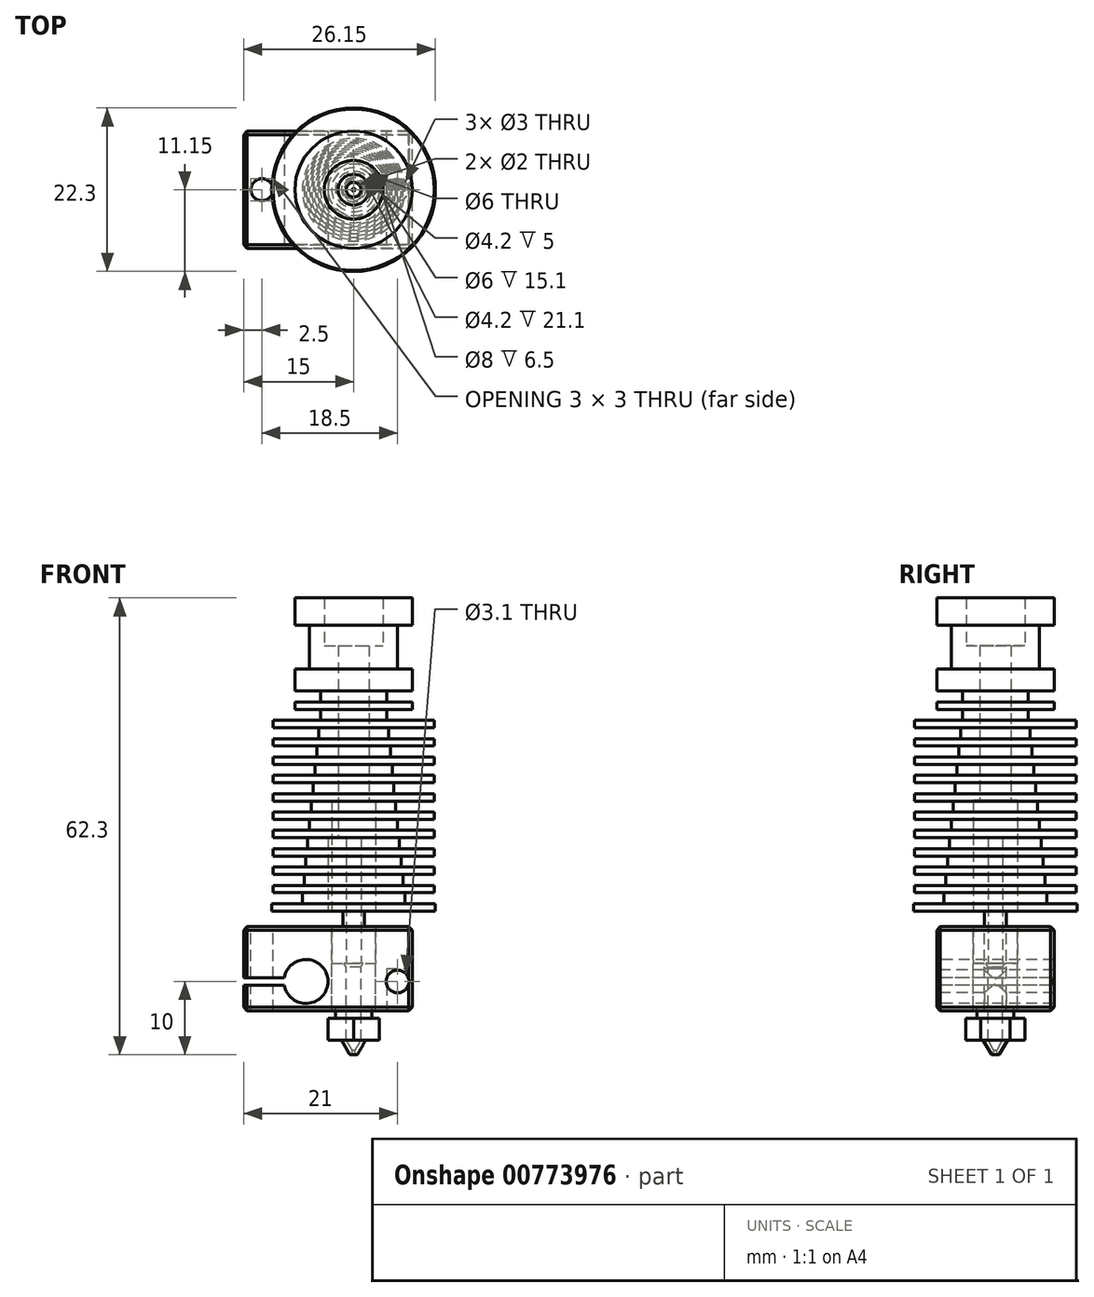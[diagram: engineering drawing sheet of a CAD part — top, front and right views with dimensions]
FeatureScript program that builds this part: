
annotation { "Feature Type Name" : "Feature", "Feature Type Description" : "" }
export const myFeature = defineFeature(function(context is Context, id is Id, definition is map)
    precondition{}
    {
        {
            var Q0;
            Q0=qCreatedBy(makeId("Front.planeOp"),FACE);
            var sketch = newSketch(context, id + "F0", { "sketchPlane" : qUnion([Q0])});
            skLineSegment(sketch, "E0", {"start": v(0, 0) * mm, "end": v(0, 45.21) * mm, "construction": true});
            skLineSegment(sketch, "E1", {"start": v(-3, 0) * mm, "end": v(-3, 15.1) * mm});
            skLineSegment(sketch, "E2", {"start": v(-3, 15.1) * mm, "end": v(-2.1, 15.1) * mm});
            skLineSegment(sketch, "E3", {"start": v(-2.1, 36.2) * mm, "end": v(-4, 36.2) * mm});
            skLineSegment(sketch, "E4", {"start": v(-4, 36.2) * mm, "end": v(-4, 42.7) * mm});
            skLineSegment(sketch, "E5", {"start": v(-4, 42.7) * mm, "end": v(-8, 42.7) * mm});
            skLineSegment(sketch, "E6", {"start": v(-8, 42.7) * mm, "end": v(-8, 39) * mm});
            skLineSegment(sketch, "E7", {"start": v(-6, 39) * mm, "end": v(-6, 33) * mm});
            skLineSegment(sketch, "E8", {"start": v(-6, 33) * mm, "end": v(-8, 33) * mm});
            skLineSegment(sketch, "E9", {"start": v(-8, 33) * mm, "end": v(-8, 30) * mm});
            skLineSegment(sketch, "E10", {"start": v(-8, 30) * mm, "end": v(-4.5, 30) * mm});
            skLineSegment(sketch, "E11", {"start": v(-4.5, 28.5) * mm, "end": v(-8, 28.5) * mm});
            skLineSegment(sketch, "E12", {"start": v(-8, 28.5) * mm, "end": v(-8, 27.5) * mm});
            skLineSegment(sketch, "E13", {"start": v(-8, 27.5) * mm, "end": v(-4.5, 27.5) * mm});
            skLineSegment(sketch, "E14", {"start": v(-4.5, 30) * mm, "end": v(-4.5, 28.5) * mm});
            skLineSegment(sketch, "E15", {"start": v(-8, 39) * mm, "end": v(-6, 39) * mm});
            skLineSegment(sketch, "E16", {"start": v(-2.1, 15.1) * mm, "end": v(-2.1, 36.2) * mm});
            skLineSegment(sketch, "E17", {"start": v(-11.15, 1) * mm, "end": v(-7, 1) * mm});
            skLineSegment(sketch, "E18", {"start": v(-7, 1) * mm, "end": v(-7, 2.5) * mm});
            skLineSegment(sketch, "E19", {"start": v(-7, 2.5) * mm, "end": v(-11, 2.5) * mm});
            skLineSegment(sketch, "E20", {"start": v(-11, 2.5) * mm, "end": v(-11, 3.5) * mm});
            skLineSegment(sketch, "E21", {"start": v(-11, 3.5) * mm, "end": v(-6.75, 3.5) * mm});
            skLineSegment(sketch, "E22", {"start": v(-6.75, 3.5) * mm, "end": v(-6.75, 5) * mm});
            skLineSegment(sketch, "E23", {"start": v(-6.75, 5) * mm, "end": v(-11, 5) * mm});
            skLineSegment(sketch, "E24", {"start": v(-11, 5) * mm, "end": v(-11, 6) * mm});
            skLineSegment(sketch, "E25", {"start": v(-11, 6) * mm, "end": v(-6.5, 6) * mm});
            skLineSegment(sketch, "E26", {"start": v(-6.5, 6) * mm, "end": v(-6.5, 7.5) * mm});
            skLineSegment(sketch, "E27", {"start": v(-6.5, 7.5) * mm, "end": v(-11, 7.5) * mm});
            skLineSegment(sketch, "E28", {"start": v(-11, 7.5) * mm, "end": v(-11, 8.5) * mm});
            skLineSegment(sketch, "E29", {"start": v(-11, 8.5) * mm, "end": v(-6.25, 8.5) * mm});
            skLineSegment(sketch, "E30", {"start": v(-6.25, 8.5) * mm, "end": v(-6.25, 10) * mm});
            skLineSegment(sketch, "E31", {"start": v(-6.25, 10) * mm, "end": v(-11, 10) * mm});
            skLineSegment(sketch, "E32", {"start": v(-11, 10) * mm, "end": v(-11, 11) * mm});
            skLineSegment(sketch, "E33", {"start": v(-11, 11) * mm, "end": v(-6, 11) * mm});
            skLineSegment(sketch, "E34", {"start": v(-6, 11) * mm, "end": v(-6, 12.5) * mm});
            skLineSegment(sketch, "E35", {"start": v(-6, 12.5) * mm, "end": v(-11, 12.5) * mm});
            skLineSegment(sketch, "E36", {"start": v(-11, 12.5) * mm, "end": v(-11, 13.5) * mm});
            skLineSegment(sketch, "E37", {"start": v(-11, 13.5) * mm, "end": v(-5.75, 13.5) * mm});
            skLineSegment(sketch, "E38", {"start": v(-5.75, 13.5) * mm, "end": v(-5.75, 15) * mm});
            skLineSegment(sketch, "E39", {"start": v(-5.75, 15) * mm, "end": v(-11, 15) * mm});
            skLineSegment(sketch, "E40", {"start": v(-11, 15) * mm, "end": v(-11, 16) * mm});
            skLineSegment(sketch, "E41", {"start": v(-11, 16) * mm, "end": v(-5.5, 16) * mm});
            skLineSegment(sketch, "E42", {"start": v(-5.5, 16) * mm, "end": v(-5.5, 17.5) * mm});
            skLineSegment(sketch, "E43", {"start": v(-5.5, 17.5) * mm, "end": v(-11, 17.5) * mm});
            skLineSegment(sketch, "E44", {"start": v(-11, 17.5) * mm, "end": v(-11, 18.5) * mm});
            skLineSegment(sketch, "E45", {"start": v(-11, 18.5) * mm, "end": v(-5.25, 18.5) * mm});
            skLineSegment(sketch, "E46", {"start": v(-5.25, 18.5) * mm, "end": v(-5.25, 20) * mm});
            skLineSegment(sketch, "E47", {"start": v(-5.25, 20) * mm, "end": v(-11, 20) * mm});
            skLineSegment(sketch, "E48", {"start": v(-11, 20) * mm, "end": v(-11, 21) * mm});
            skLineSegment(sketch, "E49", {"start": v(-11, 21) * mm, "end": v(-5, 21) * mm});
            skLineSegment(sketch, "E50", {"start": v(-5, 21) * mm, "end": v(-5, 22.5) * mm});
            skLineSegment(sketch, "E51", {"start": v(-5, 22.5) * mm, "end": v(-11, 22.5) * mm});
            skLineSegment(sketch, "E52", {"start": v(-11, 22.5) * mm, "end": v(-11, 23.5) * mm});
            skLineSegment(sketch, "E53", {"start": v(-11, 23.5) * mm, "end": v(-4.75, 23.5) * mm});
            skLineSegment(sketch, "E54", {"start": v(-4.75, 23.5) * mm, "end": v(-4.75, 25) * mm});
            skLineSegment(sketch, "E55", {"start": v(-4.75, 25) * mm, "end": v(-11, 25) * mm});
            skLineSegment(sketch, "E56", {"start": v(-11, 25) * mm, "end": v(-11, 26) * mm});
            skLineSegment(sketch, "E57", {"start": v(-11, 26) * mm, "end": v(-4.5, 26) * mm});
            skLineSegment(sketch, "E58", {"start": v(-4.5, 26) * mm, "end": v(-4.5, 27.5) * mm});
            skLineSegment(sketch, "E59", {"start": v(-3, 0) * mm, "end": v(-11.15, 0) * mm});
            skLineSegment(sketch, "E60", {"start": v(-11.15, 0) * mm, "end": v(-11.15, 1) * mm});
            skSolve(sketch);
        }
        {
            var Q0;
            Q0 = qSketchRegion(id + "F0", true);
            var Q1;
            Q1=sQuery(id+"F0.wireOp",EDGE,"E0");
            revolve(context, id + "F1", {"surfaceOperationType" : NewSurfaceOperationType.NEW, "entities" : qUnion([Q0]), "axis" : qUnion([Q1]), "revolveType" : RevolveType.FULL});
        }
        {
            var Q0;
            Q0=qCreatedBy(makeId("Front.planeOp"),FACE);
            var sketch = newSketch(context, id + "F2", { "sketchPlane" : qUnion([Q0])});
            skLineSegment(sketch, "E61", {"start": v(0, 0) * mm, "end": v(0, 46.31) * mm, "construction": true});
            skLineSegment(sketch, "E62", {"start": v(-3, 15) * mm, "end": v(-3, 10) * mm});
            skLineSegment(sketch, "E63", {"start": v(-3, 10) * mm, "end": v(-3.5, 10) * mm});
            skLineSegment(sketch, "E64", {"start": v(-3.5, 10) * mm, "end": v(-3.5, 0) * mm});
            skLineSegment(sketch, "E65", {"start": v(-3.5, 0) * mm, "end": v(-1.48, 0) * mm});
            skLineSegment(sketch, "E66", {"start": v(-1.48, 0) * mm, "end": v(-1.48, -2.1) * mm});
            skLineSegment(sketch, "E67", {"start": v(-1.48, -2.1) * mm, "end": v(-3, -2.1) * mm});
            skLineSegment(sketch, "E68", {"start": v(-3, -2.1) * mm, "end": v(-3, -7.1) * mm});
            skLineSegment(sketch, "E69", {"start": v(-3, -7.1) * mm, "end": v(-1, -7.1) * mm});
            skLineSegment(sketch, "E70", {"start": v(-1, -7.1) * mm, "end": v(-1, 10) * mm});
            skLineSegment(sketch, "E71", {"start": v(-1, 10) * mm, "end": v(-2.1, 10) * mm});
            skLineSegment(sketch, "E72", {"start": v(-2.1, 10) * mm, "end": v(-2.1, 15) * mm});
            skLineSegment(sketch, "E73", {"start": v(-2.1, 15) * mm, "end": v(-3, 15) * mm});
            skSolve(sketch);
        }
        {
            var Q0;
            Q0 = qSketchRegion(id + "F2", true);
            var Q1;
            Q1=sQuery(id+"F2.wireOp",EDGE,"E61");
            revolve(context, id + "F3", {"surfaceOperationType" : NewSurfaceOperationType.NEW, "entities" : qUnion([Q0]), "axis" : qUnion([Q1]), "revolveType" : RevolveType.FULL});
        }
        {
            var Q0;
            Q0=makeQuery(id+"F3.opRevolve","SWEPT_FACE",FACE,{"disambiguationData":[OSD([sQuery(id+"F2.wireOp",EDGE,"E67")])]});
            var sketch = newSketch(context, id + "F4", { "sketchPlane" : qUnion([Q0])});
            skLineSegment(sketch, "E74.bottom", {"start": v(8, -8) * mm, "end": v(-15, -8) * mm});
            skLineSegment(sketch, "E74.top", {"start": v(8, 8) * mm, "end": v(-15, 8) * mm});
            skLineSegment(sketch, "E74.left", {"start": v(8, -8) * mm, "end": v(8, 8) * mm});
            skLineSegment(sketch, "E74.right", {"start": v(-15, -8) * mm, "end": v(-15, 8) * mm});
            skLineSegment(sketch, "E75", {"start": v(-16.95, 0) * mm, "end": v(14.7, 0) * mm, "construction": true});
            skCircle(sketch, "E76", {"center": v(0, 0) * mm, "radius": 3 * mm});
            skCircle(sketch, "E77", {"center": v(6, 0) * mm, "radius": 1.5 * mm});
            skCircle(sketch, "E78", {"center": v(-12.5, 0) * mm, "radius": 1.5 * mm});
            skSolve(sketch);
        }
        {
            var Q0;
            Q0 = qSketchRegion(id + "F4", true);
            var Q1;
            Q1=makeQuery(id+"F4.imprint","IMPRINT",FACE,{"disambiguationData":[TD([[makeQuery(id+"F4.imprint","IMPRINT",EDGE,{"derivedFrom":sQuery(id+"F4.wireOp",EDGE,"E77")}),1.0]])]});
            extrude(context, id + "F5", {"entities" : qUnion([Q0, Q1]), "oppositeDirection" : true, "depth" : 11.5 * mm, "offsetDistance" : 25 * mm});
        }
        {
            var Q0;
            Q0=makeQuery(id+"F5.opExtrude","CAP_FACE",FACE,{"disambiguationData":[OSD([sQuery(id+"F4.wireOp",EDGE,"E74.bottom"),sQuery(id+"F4.wireOp",EDGE,"E74.top"),sQuery(id+"F4.wireOp",EDGE,"E74.left"),sQuery(id+"F4.wireOp",EDGE,"E74.right"),sQuery(id+"F4.wireOp",EDGE,"E76"),sQuery(id+"F4.wireOp",EDGE,"E78")])],"isStart":false});
            var sketch = newSketch(context, id + "F6", { "sketchPlane" : qUnion([Q0])});
            skCircle(sketch, "E79.0", {"center": v(6, 0) * mm, "radius": 1.5 * mm});
            skSolve(sketch);
        }
        {
            var Q0;
            Q0 = qSketchRegion(id + "F6", true);
            extrude(context, id + "F7", {"entities" : qUnion([Q0]), "operationType" : NewBodyOperationType.REMOVE, "oppositeDirection" : true, "depth" : 5.75 * mm, "offsetDistance" : 25 * mm});
        }
        {
            var Q0;
            Q0=makeQuery(id+"F5.opExtrude","SWEPT_FACE",FACE,{"disambiguationData":[OSD([sQuery(id+"F4.wireOp",EDGE,"E74.bottom")])]});
            var sketch = newSketch(context, id + "F8", { "sketchPlane" : qUnion([Q0])});
            skLineSegment(sketch, "E80", {"start": v(-15.75, -9.6) * mm, "end": v(10.37, -9.6) * mm, "construction": true});
            skCircle(sketch, "E81", {"center": v(-6.5, -9.6) * mm, "radius": 3 * mm});
            skCircle(sketch, "E82", {"center": v(6, -9.6) * mm, "radius": 1.55 * mm});
            skLineSegment(sketch, "E83", {"start": v(-15, -10.1) * mm, "end": v(-9.46, -10.1) * mm});
            skPoint(sketch, "E84.startSnap0", {"position": v(-15, -7.85) * mm});
            skLineSegment(sketch, "E85", {"start": v(-15, -10.1) * mm, "end": v(-15, -9.1) * mm});
            skLineSegment(sketch, "E86", {"start": v(-15, -9.1) * mm, "end": v(-9.46, -9.1) * mm});
            skSolve(sketch);
        }
        {
            var Q0;
            Q0 = qSketchRegion(id + "F8", true);
            var Q1;
            Q1=makeQuery(id+"F5.opExtrude","SWEPT_FACE",FACE,{"disambiguationData":[OSD([sQuery(id+"F4.wireOp",EDGE,"E74.top")])]});
            extrude(context, id + "F9", {"entities" : qUnion([Q0]), "operationType" : NewBodyOperationType.REMOVE, "endBound" : BoundingType.UP_TO_SURFACE, "oppositeDirection" : true, "depth" : 25 * mm, "endBoundEntityFace" : qUnion([Q1]), "offsetDistance" : 25 * mm});
        }
        {
            var Q0;
            Q0=makeQuery(id+"F5.opExtrude","CAP_EDGE",EDGE,{"disambiguationData":[OSD([sQuery(id+"F4.wireOp",EDGE,"E74.bottom")])],"isStart":true});
            var Q1;
            Q1=makeQuery(id+"F5.opExtrude","CAP_EDGE",EDGE,{"disambiguationData":[OSD([sQuery(id+"F4.wireOp",EDGE,"E74.right")])],"isStart":true});
            var Q2;
            {var subQ0=sQuery(id+"F4.wireOp",EDGE,"E74.bottom");var subQ1=sQuery(id+"F4.wireOp",EDGE,"E74.right");Q2=makeQuery(id+"F9.boolean.opBoolean","SPLIT",EDGE,{"disambiguationData":[TD([makeQuery(id+"F9.opExtrude","SWEPT_FACE",FACE,{"disambiguationData":[OSD([sQuery(id+"F8.wireOp",EDGE,"E86")])]})])],"derivedFrom":makeQuery(id+"F5.opExtrude","SWEPT_EDGE",EDGE,{"disambiguationData":[OSD([subQ0,subQ1])]})});}
            var Q3;
            {var subQ0=sQuery(id+"F4.wireOp",EDGE,"E74.bottom");var subQ1=sQuery(id+"F4.wireOp",EDGE,"E74.right");Q3=makeQuery(id+"F9.boolean.opBoolean","SPLIT",EDGE,{"disambiguationData":[TD([makeQuery(id+"F9.opExtrude","SWEPT_FACE",FACE,{"disambiguationData":[OSD([sQuery(id+"F8.wireOp",EDGE,"E83")])]})])],"derivedFrom":makeQuery(id+"F5.opExtrude","SWEPT_EDGE",EDGE,{"disambiguationData":[OSD([subQ0,subQ1])]})});}
            var Q4;
            Q4=makeQuery(id+"F5.opExtrude","SWEPT_EDGE",EDGE,{"disambiguationData":[OSD([sQuery(id+"F4.wireOp",EDGE,"E74.bottom"),sQuery(id+"F4.wireOp",EDGE,"E74.left")])]});
            var Q5;
            Q5=makeQuery(id+"F5.opExtrude","CAP_EDGE",EDGE,{"disambiguationData":[OSD([sQuery(id+"F4.wireOp",EDGE,"E74.bottom")])],"isStart":false});
            var Q6;
            Q6=makeQuery(id+"F5.opExtrude","CAP_EDGE",EDGE,{"disambiguationData":[OSD([sQuery(id+"F4.wireOp",EDGE,"E74.right")])],"isStart":false});
            var Q7;
            Q7=makeQuery(id+"F5.opExtrude","CAP_EDGE",EDGE,{"disambiguationData":[OSD([sQuery(id+"F4.wireOp",EDGE,"E74.left")])],"isStart":false});
            var Q8;
            Q8=makeQuery(id+"F5.opExtrude","CAP_EDGE",EDGE,{"disambiguationData":[OSD([sQuery(id+"F4.wireOp",EDGE,"E74.left")])],"isStart":true});
            var Q9;
            Q9=makeQuery(id+"F5.opExtrude","SWEPT_EDGE",EDGE,{"disambiguationData":[OSD([sQuery(id+"F4.wireOp",EDGE,"E74.top"),sQuery(id+"F4.wireOp",EDGE,"E74.left")])]});
            var Q10;
            Q10=makeQuery(id+"F5.opExtrude","CAP_EDGE",EDGE,{"disambiguationData":[OSD([sQuery(id+"F4.wireOp",EDGE,"E74.top")])],"isStart":true});
            var Q11;
            Q11=makeQuery(id+"F5.opExtrude","CAP_EDGE",EDGE,{"disambiguationData":[OSD([sQuery(id+"F4.wireOp",EDGE,"E74.top")])],"isStart":false});
            var Q12;
            {var subQ0=sQuery(id+"F4.wireOp",EDGE,"E74.right");var subQ1=sQuery(id+"F4.wireOp",EDGE,"E74.top");Q12=makeQuery(id+"F9.boolean.opBoolean","SPLIT",EDGE,{"disambiguationData":[TD([makeQuery(id+"F9.opExtrude","SWEPT_FACE",FACE,{"disambiguationData":[OSD([sQuery(id+"F8.wireOp",EDGE,"E83")])]})])],"derivedFrom":makeQuery(id+"F5.opExtrude","SWEPT_EDGE",EDGE,{"disambiguationData":[OSD([subQ1,subQ0])]})});}
            var Q13;
            {var subQ0=sQuery(id+"F4.wireOp",EDGE,"E74.right");var subQ1=sQuery(id+"F4.wireOp",EDGE,"E74.top");Q13=makeQuery(id+"F9.boolean.opBoolean","SPLIT",EDGE,{"disambiguationData":[TD([makeQuery(id+"F9.opExtrude","SWEPT_FACE",FACE,{"disambiguationData":[OSD([sQuery(id+"F8.wireOp",EDGE,"E86")])]})])],"derivedFrom":makeQuery(id+"F5.opExtrude","SWEPT_EDGE",EDGE,{"disambiguationData":[OSD([subQ1,subQ0])]})});}
            chamfer(context, id + "F10", {"entities" : qUnion([Q0, Q1, Q2, Q3, Q4, Q5, Q6, Q7, Q8, Q9, Q10, Q11, Q12, Q13]), "width" : .5 * mm, "tangentPropagation" : true});
        }
        {
            var Q0;
            Q0=qCreatedBy(makeId("Front.planeOp"),FACE);
            var sketch = newSketch(context, id + "F11", { "sketchPlane" : qUnion([Q0])});
            skLineSegment(sketch, "E87", {"start": v(0, 0) * mm, "end": v(0, -17.7) * mm, "construction": true});
            skLineSegment(sketch, "E88", {"start": v(-1.3, -7.1) * mm, "end": v(-3, -7.1) * mm});
            skLineSegment(sketch, "E89", {"start": v(-3, -7.1) * mm, "end": v(-3, -13.1) * mm});
            skLineSegment(sketch, "E90", {"start": v(-3, -13.1) * mm, "end": v(-2.5, -13.1) * mm});
            skLineSegment(sketch, "E91", {"start": v(-2.5, -13.1) * mm, "end": v(-2.5, -14.6) * mm});
            skLineSegment(sketch, "E92", {"start": v(-2.5, -14.6) * mm, "end": v(-6, -14.6) * mm});
            skLineSegment(sketch, "E93", {"start": v(-6, -14.6) * mm, "end": v(-6, -17.6) * mm});
            skLineSegment(sketch, "E94", {"start": v(-6, -17.6) * mm, "end": v(-1.65, -17.6) * mm});
            skLineSegment(sketch, "E95", {"start": v(-1.65, -17.6) * mm, "end": v(-0.5, -19.6) * mm});
            skLineSegment(sketch, "E96", {"start": v(-0.5, -19.6) * mm, "end": v(-0.2, -19.6) * mm});
            skLineSegment(sketch, "E97", {"start": v(-0.2, -19.6) * mm, "end": v(-0.2, -19) * mm});
            skLineSegment(sketch, "E98", {"start": v(-0.2, -19) * mm, "end": v(-1, -17.61) * mm});
            skLineSegment(sketch, "E99", {"start": v(-1, -17.61) * mm, "end": v(-1, -7.62) * mm});
            skLineSegment(sketch, "E100", {"start": v(-1, -7.62) * mm, "end": v(-1.3, -7.1) * mm});
            skSolve(sketch);
        }
        {
            var Q0;
            Q0 = qSketchRegion(id + "F11", true);
            var Q1;
            Q1=sQuery(id+"F11.wireOp",EDGE,"E87");
            revolve(context, id + "F12", {"surfaceOperationType" : NewSurfaceOperationType.NEW, "entities" : qUnion([Q0]), "axis" : qUnion([Q1]), "revolveType" : RevolveType.FULL});
        }
        {
            var Q0;
            Q0=makeQuery(id+"F12.opRevolve","SWEPT_FACE",FACE,{"disambiguationData":[OSD([sQuery(id+"F11.wireOp",EDGE,"E94")])]});
            var sketch = newSketch(context, id + "F13", { "sketchPlane" : qUnion([Q0])});
            skCircle(sketch, "E101.cCircle", {"center": v(0, 0) * mm, "radius": 3.5 * mm, "construction": true});
            skLineSegment(sketch, "E101.0", {"start": v(3.5, -2.02) * mm, "end": v(0, -4.04) * mm});
            skLineSegment(sketch, "E101.1", {"start": v(0, -4.04) * mm, "end": v(-3.5, -2.02) * mm});
            skLineSegment(sketch, "E101.2", {"start": v(-3.5, -2.02) * mm, "end": v(-3.5, 2.02) * mm});
            skLineSegment(sketch, "E101.3", {"start": v(-3.5, 2.02) * mm, "end": v(0, 4.04) * mm});
            skLineSegment(sketch, "E101.4", {"start": v(0, 4.04) * mm, "end": v(3.5, 2.02) * mm});
            skLineSegment(sketch, "E101.5", {"start": v(3.5, 2.02) * mm, "end": v(3.5, -2.02) * mm});
            skPoint(sketch, "E101.0.midPoint", {"position": v(1.75, -3.03) * mm});
            skLineSegment(sketch, "E102", {"start": v(0, 0) * mm, "end": v(0, 18.08) * mm, "construction": true});
            skCircle(sketch, "E103", {"center": v(0, 0) * mm, "radius": 6.55 * mm});
            skSolve(sketch);
        }
        {
            var Q0;
            Q0 = qSketchRegion(id + "F13", true);
            var Q1;
            Q1=makeQuery(id+"F12.opRevolve","SWEPT_FACE",FACE,{"disambiguationData":[OSD([sQuery(id+"F11.wireOp",EDGE,"E92")])]});
            extrude(context, id + "F14", {"entities" : qUnion([Q0]), "operationType" : NewBodyOperationType.REMOVE, "endBound" : BoundingType.UP_TO_SURFACE, "oppositeDirection" : true, "depth" : 25 * mm, "endBoundEntityFace" : qUnion([Q1]), "offsetDistance" : 25 * mm});
        }
        {
            var Q0;
            Q0=makeQuery(id+"F12.opRevolve","SWEPT_EDGE",EDGE,{"disambiguationData":[OSD([sQuery(id+"F11.wireOp",EDGE,"E95"),sQuery(id+"F11.wireOp",EDGE,"E96")])]});
            fillet(context, id + "F15", {"entities" : qUnion([Q0]), "radius" : .2 * mm, "tangentPropagation" : true, "allowEdgeOverflow" : false});
        }
    });
